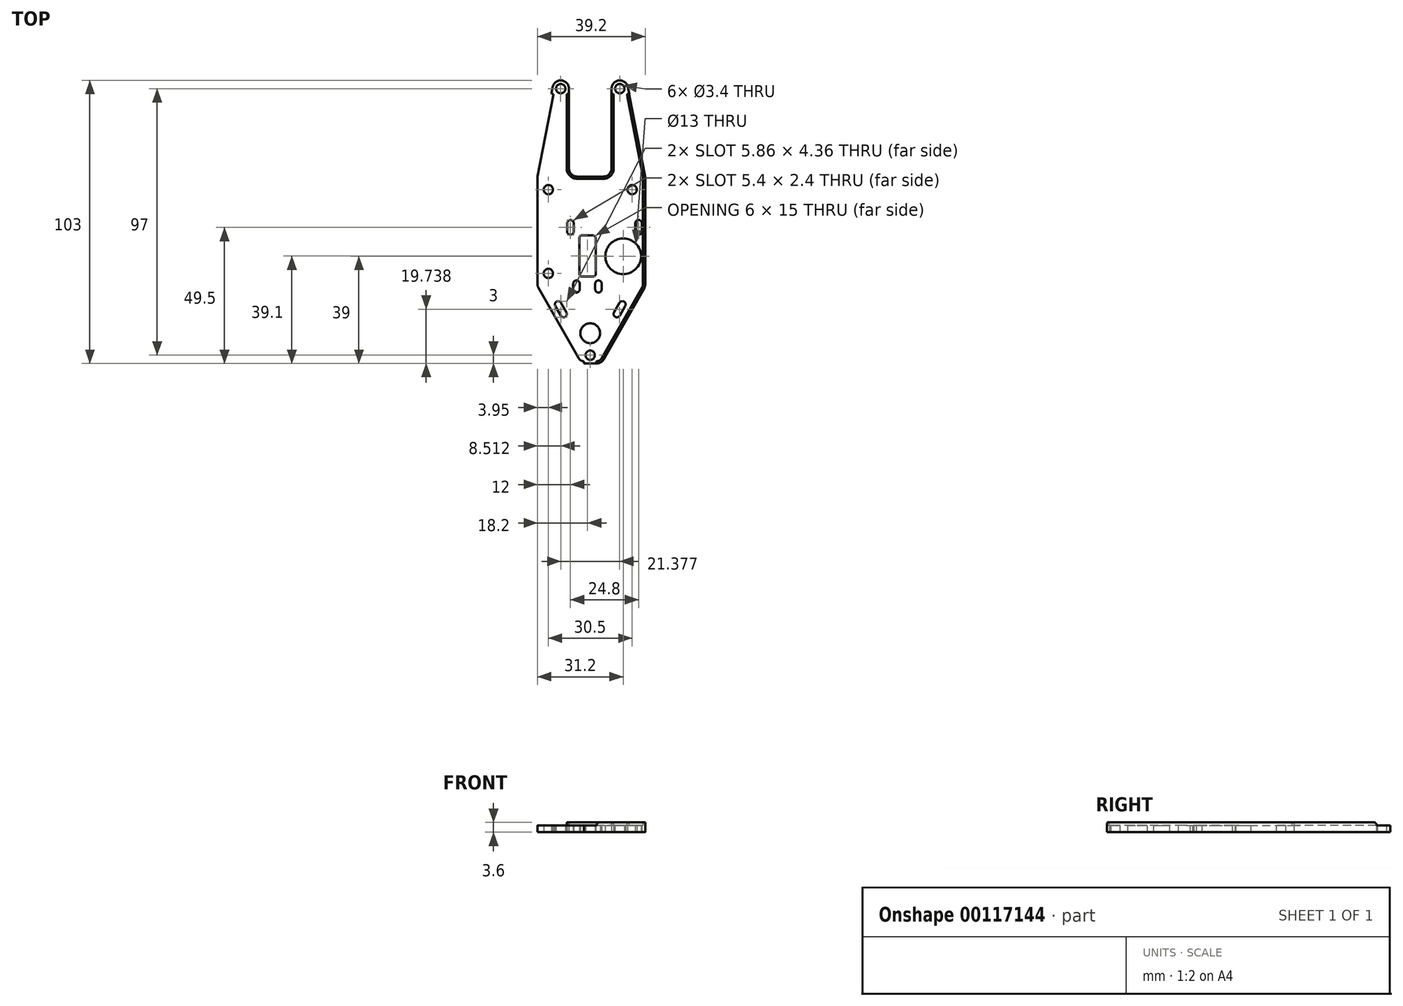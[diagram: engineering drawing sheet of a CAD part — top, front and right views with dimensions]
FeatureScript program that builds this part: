
annotation { "Feature Type Name" : "Feature", "Feature Type Description" : "" }
export const myFeature = defineFeature(function(context is Context, id is Id, definition is map)
    precondition{}
    {
        {
            var Q0;
            Q0=qCreatedBy(makeId("Top.planeOp"),FACE);
            var sketch = newSketch(context, id + "F0", { "sketchPlane" : qUnion([Q0])});
            skCircle(sketch, "E0", {"center": v(10.75, 52) * mm, "radius": 1.7 * mm});
            skCircle(sketch, "E1", {"center": v(15.25, 15.25) * mm, "radius": 1.7 * mm});
            skCircle(sketch, "E2", {"center": v(0, -45) * mm, "radius": 1.7 * mm});
            skCircle(sketch, "E3", {"center": v(0, -37) * mm, "radius": 3.6 * mm});
            skLineSegment(sketch, "E4", {"start": v(20, 0) * mm, "end": v(20, 19.71) * mm});
            skLineSegment(sketch, "E5", {"start": v(10.75, 55) * mm, "end": v(10.75, 55) * mm});
            skLineSegment(sketch, "E6", {"start": v(7.75, 52) * mm, "end": v(7.75, 23) * mm});
            skLineSegment(sketch, "E7", {"start": v(4.75, 20) * mm, "end": v(0, 20) * mm});
            skLineSegment(sketch, "E8", {"start": v(13.7, 52.57) * mm, "end": v(19.95, 20.28) * mm});
            skPoint(sketch, "E9.visualSharp", {"position": v(7.75, 55) * mm});
            skArc(sketch, "E9.filletArc", {"start": v(10.75, 55) * mm, "mid": v(8.63, 54.12) * mm, "end": v(7.75, 52) * mm});
            skPoint(sketch, "E10.visualSharp", {"position": v(13.22, 55) * mm});
            skArc(sketch, "E10.filletArc", {"start": v(13.7, 52.57) * mm, "mid": v(12.66, 54.31) * mm, "end": v(10.75, 55) * mm});
            skPoint(sketch, "E11.visualSharp", {"position": v(7.75, 20) * mm});
            skArc(sketch, "E11.filletArc", {"start": v(4.75, 20) * mm, "mid": v(6.87, 20.88) * mm, "end": v(7.75, 23) * mm});
            skCircle(sketch, "E12.MirrorC", {"center": v(15.25, -15.25) * mm, "radius": 1.7 * mm, "construction": true});
            skLineSegment(sketch, "E13.MirrorCS", {"start": v(20, 0) * mm, "end": v(20, -19.2) * mm});
            skLineSegment(sketch, "E14", {"start": v(0, -48) * mm, "end": v(2.3, -48) * mm});
            skLineSegment(sketch, "E15", {"start": v(19.6, -20.7) * mm, "end": v(4.9, -46.49) * mm});
            skPoint(sketch, "E16.visualSharp", {"position": v(4.05, -48) * mm});
            skArc(sketch, "E16.filletArc", {"start": v(2.3, -48) * mm, "mid": v(3.8, -47.6) * mm, "end": v(4.9, -46.49) * mm});
            skPoint(sketch, "E17.visualSharp", {"position": v(20, -20) * mm});
            skArc(sketch, "E17.filletArc", {"start": v(19.6, -20.7) * mm, "mid": v(19.9, -19.97) * mm, "end": v(20, -19.2) * mm});
            skLineSegment(sketch, "E18", {"start": v(9.7, -30) * mm, "end": v(11.68, -26.52) * mm, "construction": true});
            skArc(sketch, "E19.0.startCap", {"start": v(10.74, -30.6) * mm, "mid": v(9.1, -31.04) * mm, "end": v(8.66, -29.4) * mm});
            skArc(sketch, "E19.0.endCap", {"start": v(10.64, -25.93) * mm, "mid": v(12.27, -25.48) * mm, "end": v(12.72, -27.12) * mm});
            skLineSegment(sketch, "E19.0.left", {"start": v(8.66, -29.4) * mm, "end": v(10.64, -25.93) * mm});
            skLineSegment(sketch, "E19.0.right", {"start": v(10.74, -30.6) * mm, "end": v(12.72, -27.12) * mm});
            skPoint(sketch, "E20.visualSharp", {"position": v(20, 20) * mm});
            skArc(sketch, "E20.filletArc", {"start": v(20, 19.71) * mm, "mid": v(19.99, 20) * mm, "end": v(19.95, 20.28) * mm});
            skArc(sketch, "E21.MirrorCS", {"start": v(-19.6, -20.7) * mm, "mid": v(-19.9, -19.97) * mm, "end": v(-20, -19.2) * mm});
            skArc(sketch, "E22.MirrorCS", {"start": v(-20, 19.71) * mm, "mid": v(-19.99, 20) * mm, "end": v(-19.95, 20.28) * mm});
            skArc(sketch, "E23.MirrorCS", {"start": v(-10.74, -30.6) * mm, "mid": v(-9.1, -31.04) * mm, "end": v(-8.66, -29.4) * mm});
            skLineSegment(sketch, "E24.MirrorCS", {"start": v(-8.66, -29.4) * mm, "end": v(-10.64, -25.93) * mm});
            skArc(sketch, "E25.MirrorCS", {"start": v(-13.7, 52.57) * mm, "mid": v(-12.66, 54.31) * mm, "end": v(-10.75, 55) * mm});
            skCircle(sketch, "E26.MirrorC", {"center": v(-10.75, 52) * mm, "radius": 1.7 * mm});
            skArc(sketch, "E27.MirrorCS", {"start": v(-2.3, -48) * mm, "mid": v(-3.8, -47.6) * mm, "end": v(-4.9, -46.49) * mm});
            skLineSegment(sketch, "E28.MirrorCS", {"start": v(-9.7, -30) * mm, "end": v(-11.68, -26.52) * mm, "construction": true});
            skArc(sketch, "E29.MirrorCS", {"start": v(-10.64, -25.93) * mm, "mid": v(-12.27, -25.48) * mm, "end": v(-12.72, -27.12) * mm});
            skLineSegment(sketch, "E30.MirrorCS", {"start": v(-10.74, -30.6) * mm, "end": v(-12.72, -27.12) * mm});
            skArc(sketch, "E31.MirrorCS", {"start": v(-4.75, 20) * mm, "mid": v(-6.87, 20.88) * mm, "end": v(-7.75, 23) * mm});
            skArc(sketch, "E32.MirrorCS", {"start": v(-10.75, 55) * mm, "mid": v(-8.63, 54.12) * mm, "end": v(-7.75, 52) * mm});
            skLineSegment(sketch, "E33.MirrorCS", {"start": v(0, -48) * mm, "end": v(-2.3, -48) * mm});
            skPoint(sketch, "E34.MirrorP", {"position": v(-20, 20) * mm});
            skLineSegment(sketch, "E35.MirrorCS", {"start": v(-10.75, 55) * mm, "end": v(-10.75, 55) * mm});
            skLineSegment(sketch, "E36.MirrorCS", {"start": v(-20, 0) * mm, "end": v(-20, -19.2) * mm});
            skCircle(sketch, "E37.MirrorC", {"center": v(-15.25, -15.25) * mm, "radius": 1.7 * mm});
            skLineSegment(sketch, "E38.MirrorCS", {"start": v(-13.7, 52.57) * mm, "end": v(-19.95, 20.28) * mm});
            skLineSegment(sketch, "E39.MirrorCS", {"start": v(-4.75, 20) * mm, "end": v(0, 20) * mm});
            skLineSegment(sketch, "E40.MirrorCS", {"start": v(-20, 0) * mm, "end": v(-20, 19.71) * mm});
            skLineSegment(sketch, "E41.MirrorCS", {"start": v(-7.75, 52) * mm, "end": v(-7.75, 23) * mm});
            skCircle(sketch, "E42.MirrorC", {"center": v(-15.25, 15.25) * mm, "radius": 1.7 * mm});
            skPoint(sketch, "E43.MirrorP", {"position": v(-4.05, -48) * mm});
            skLineSegment(sketch, "E44.MirrorCS", {"start": v(-19.6, -20.7) * mm, "end": v(-4.9, -46.49) * mm});
            skPoint(sketch, "E45.MirrorP", {"position": v(-7.75, 55) * mm});
            skPoint(sketch, "E46.MirrorP", {"position": v(-13.22, 55) * mm});
            skPoint(sketch, "E47.MirrorP", {"position": v(-7.75, 20) * mm});
            skPoint(sketch, "E48.MirrorP", {"position": v(-20, -20) * mm});
            skLineSegment(sketch, "E49.bottom", {"start": v(-3, -1.4) * mm, "end": v(1, -1.4) * mm});
            skLineSegment(sketch, "E49.top", {"start": v(-3, -16.4) * mm, "end": v(1, -16.4) * mm});
            skLineSegment(sketch, "E49.left", {"start": v(-4, -2.4) * mm, "end": v(-4, -15.4) * mm});
            skLineSegment(sketch, "E49.right", {"start": v(2, -2.4) * mm, "end": v(2, -15.4) * mm});
            skPoint(sketch, "E50.visualSharp", {"position": v(-4, -1.4) * mm});
            skArc(sketch, "E50.filletArc", {"start": v(-3, -1.4) * mm, "mid": v(-3.7, -1.7) * mm, "end": v(-4, -2.4) * mm});
            skPoint(sketch, "E51.visualSharp", {"position": v(2, -16.4) * mm});
            skArc(sketch, "E51.filletArc", {"start": v(1, -16.4) * mm, "mid": v(1.7, -16.1) * mm, "end": v(2, -15.4) * mm});
            skPoint(sketch, "E52.visualSharp", {"position": v(-4, -16.4) * mm});
            skArc(sketch, "E52.filletArc", {"start": v(-4, -15.4) * mm, "mid": v(-3.7, -16.1) * mm, "end": v(-3, -16.4) * mm});
            skPoint(sketch, "E53.visualSharp", {"position": v(2, -1.4) * mm});
            skArc(sketch, "E53.filletArc", {"start": v(2, -2.4) * mm, "mid": v(1.7, -1.7) * mm, "end": v(1, -1.4) * mm});
            skCircle(sketch, "E54", {"center": v(12, -9) * mm, "radius": 6.5 * mm});
            skArc(sketch, "E55.0", {"start": v(18.91, -20.3) * mm, "mid": v(19.13, -19.77) * mm, "end": v(19.2, -19.2) * mm});
            skLineSegment(sketch, "E55.1", {"start": v(19.2, 0) * mm, "end": v(19.2, -19.2) * mm});
            skLineSegment(sketch, "E55.2", {"start": v(19.2, 0) * mm, "end": v(19.2, 19.71) * mm});
            skLineSegment(sketch, "E55.3", {"start": v(-13.38, 50) * mm, "end": v(-19.16, 20.13) * mm});
            skArc(sketch, "E55.4", {"start": v(-19.2, 19.71) * mm, "mid": v(-19.19, 19.92) * mm, "end": v(-19.16, 20.13) * mm});
            skLineSegment(sketch, "E55.5", {"start": v(-19.2, 0) * mm, "end": v(-19.2, 19.71) * mm});
            skLineSegment(sketch, "E55.6", {"start": v(-19.2, 0) * mm, "end": v(-19.2, -19.2) * mm});
            skArc(sketch, "E55.7", {"start": v(-18.91, -20.3) * mm, "mid": v(-19.13, -19.77) * mm, "end": v(-19.2, -19.2) * mm});
            skLineSegment(sketch, "E55.8", {"start": v(-18.91, -20.3) * mm, "end": v(-4.21, -46.09) * mm});
            skArc(sketch, "E55.9", {"start": v(2.3, -47.2) * mm, "mid": v(3.4, -46.9) * mm, "end": v(4.21, -46.09) * mm});
            skArc(sketch, "E55.12", {"start": v(-2.3, -47.2) * mm, "mid": v(-3.4, -46.9) * mm, "end": v(-4.21, -46.09) * mm});
            skLineSegment(sketch, "E55.15", {"start": v(-8.55, 50) * mm, "end": v(-8.55, 23) * mm});
            skLineSegment(sketch, "E55.16", {"start": v(18.91, -20.3) * mm, "end": v(4.21, -46.09) * mm});
            skArc(sketch, "E55.17", {"start": v(-4.75, 19.2) * mm, "mid": v(-7.44, 20.31) * mm, "end": v(-8.55, 23) * mm});
            skLineSegment(sketch, "E55.18", {"start": v(-4.75, 19.2) * mm, "end": v(0, 19.2) * mm});
            skLineSegment(sketch, "E55.19", {"start": v(4.75, 19.2) * mm, "end": v(0, 19.2) * mm});
            skArc(sketch, "E55.20", {"start": v(4.75, 19.2) * mm, "mid": v(7.44, 20.31) * mm, "end": v(8.55, 23) * mm});
            skLineSegment(sketch, "E55.21", {"start": v(8.55, 50) * mm, "end": v(8.55, 23) * mm});
            skLineSegment(sketch, "E55.24", {"start": v(13.38, 50) * mm, "end": v(19.16, 20.13) * mm});
            skArc(sketch, "E55.25", {"start": v(19.2, 19.71) * mm, "mid": v(19.19, 19.92) * mm, "end": v(19.16, 20.13) * mm});
            skLineSegment(sketch, "E56", {"start": v(-2.3, -47.2) * mm, "end": v(-2.3, -48) * mm});
            skLineSegment(sketch, "E57", {"start": v(2.3, -47.2) * mm, "end": v(2.3, -48) * mm});
            skLineSegment(sketch, "E58", {"start": v(-24.48, 50) * mm, "end": v(27.62, 50) * mm, "construction": true});
            skLineSegment(sketch, "E59", {"start": v(-8.55, 50) * mm, "end": v(-7.75, 50) * mm});
            skLineSegment(sketch, "E60", {"start": v(7.75, 50) * mm, "end": v(8.55, 50) * mm});
            skLineSegment(sketch, "E61", {"start": v(13.38, 50) * mm, "end": v(14.16, 50.15) * mm});
            skLineSegment(sketch, "E62", {"start": v(-13.38, 50) * mm, "end": v(-14.16, 50.15) * mm});
            skLineSegment(sketch, "E63", {"start": v(-7.2, 3) * mm, "end": v(-7.2, 0) * mm, "construction": true});
            skArc(sketch, "E64.0.startCap", {"start": v(-8.4, 3) * mm, "mid": v(-7.2, 4.2) * mm, "end": v(-6, 3) * mm});
            skArc(sketch, "E64.0.endCap", {"start": v(-6, 0) * mm, "mid": v(-7.2, -1.2) * mm, "end": v(-8.4, 0) * mm});
            skLineSegment(sketch, "E64.0.left", {"start": v(-6, 3) * mm, "end": v(-6, 0) * mm});
            skLineSegment(sketch, "E64.0.right", {"start": v(-8.4, 3) * mm, "end": v(-8.4, 0) * mm});
            skLineSegment(sketch, "E65", {"start": v(17.6, 0) * mm, "end": v(17.6, 3) * mm, "construction": true});
            skArc(sketch, "E66.0.startCap", {"start": v(18.8, 0) * mm, "mid": v(17.6, -1.2) * mm, "end": v(16.4, 0) * mm});
            skArc(sketch, "E66.0.endCap", {"start": v(16.4, 3) * mm, "mid": v(17.6, 4.2) * mm, "end": v(18.8, 3) * mm});
            skLineSegment(sketch, "E66.0.left", {"start": v(16.4, 0) * mm, "end": v(16.4, 3) * mm});
            skLineSegment(sketch, "E66.0.right", {"start": v(18.8, 0) * mm, "end": v(18.8, 3) * mm});
            skLineSegment(sketch, "E67", {"start": v(3, -19) * mm, "end": v(3, -21) * mm, "construction": true});
            skLineSegment(sketch, "E68", {"start": v(-5, -19) * mm, "end": v(-5, -21) * mm, "construction": true});
            skArc(sketch, "E69.0.startCap", {"start": v(1.8, -19) * mm, "mid": v(3, -17.8) * mm, "end": v(4.2, -19) * mm});
            skArc(sketch, "E69.0.endCap", {"start": v(4.2, -21) * mm, "mid": v(3, -22.2) * mm, "end": v(1.8, -21) * mm});
            skLineSegment(sketch, "E69.0.left", {"start": v(4.2, -19) * mm, "end": v(4.2, -21) * mm});
            skLineSegment(sketch, "E69.0.right", {"start": v(1.8, -19) * mm, "end": v(1.8, -21) * mm});
            skArc(sketch, "E69.1.startCap", {"start": v(-6.2, -19) * mm, "mid": v(-5, -17.8) * mm, "end": v(-3.8, -19) * mm});
            skArc(sketch, "E69.1.endCap", {"start": v(-3.8, -21) * mm, "mid": v(-5, -22.2) * mm, "end": v(-6.2, -21) * mm});
            skLineSegment(sketch, "E69.1.left", {"start": v(-3.8, -19) * mm, "end": v(-3.8, -21) * mm});
            skLineSegment(sketch, "E69.1.right", {"start": v(-6.2, -19) * mm, "end": v(-6.2, -21) * mm});
            skSolve(sketch);
        }
        {
            var Q0;
            Q0=makeQuery(id+"F0.imprint","IMPRINT",FACE,{"disambiguationData":[TD([[makeQuery(id+"F0.imprint","IMPRINT",EDGE,{"derivedFrom":sQuery(id+"F0.wireOp",EDGE,"E0")}),-1.0]])]});
            extrude(context, id + "F1", {"entities" : qUnion([Q0]), "depth" : 2.4 * mm});
        }
        {
            var Q0;
            Q0=makeQuery(id+"F0.imprint","IMPRINT",FACE,{"disambiguationData":[TD([[makeQuery(id+"F0.imprint","IMPRINT",EDGE,{"derivedFrom":sQuery(id+"F0.wireOp",EDGE,"E4")}),1.0]])]});
            var Q1;
            Q1=makeQuery(id+"F0.imprint","IMPRINT",FACE,{"disambiguationData":[TD([[makeQuery(id+"F0.imprint","IMPRINT",EDGE,{"derivedFrom":sQuery(id+"F0.wireOp",EDGE,"E7")}),1.0]])]});
            var Q2;
            Q2=makeQuery(id+"F0.imprint","IMPRINT",FACE,{"disambiguationData":[TD([[makeQuery(id+"F0.imprint","IMPRINT",EDGE,{"derivedFrom":sQuery(id+"F0.wireOp",EDGE,"E21.MirrorCS")}),-1.0]])]});
            extrude(context, id + "F2", {"entities" : qUnion([Q0, Q1, Q2]), "operationType" : NewBodyOperationType.ADD, "depth" : 3.6 * mm});
        }
        {
            var Q0;
            Q0=makeQuery(id+"F2.opExtrude","CAP_EDGE",EDGE,{"disambiguationData":[OSD([sQuery(id+"F0.wireOp",EDGE,"E62")])],"isStart":false});
            var Q1;
            Q1=makeQuery(id+"F2.opExtrude","CAP_EDGE",EDGE,{"disambiguationData":[OSD([sQuery(id+"F0.wireOp",EDGE,"E59")])],"isStart":false});
            var Q2;
            Q2=makeQuery(id+"F2.opExtrude","CAP_EDGE",EDGE,{"disambiguationData":[OSD([sQuery(id+"F0.wireOp",EDGE,"E60")])],"isStart":false});
            var Q3;
            Q3=makeQuery(id+"F2.opExtrude","CAP_EDGE",EDGE,{"disambiguationData":[OSD([sQuery(id+"F0.wireOp",EDGE,"E61")])],"isStart":false});
            var Q4;
            Q4=makeQuery(id+"F2.opExtrude","CAP_EDGE",EDGE,{"disambiguationData":[OSD([sQuery(id+"F0.wireOp",EDGE,"E56")])],"isStart":false});
            var Q5;
            Q5=makeQuery(id+"F2.opExtrude","CAP_EDGE",EDGE,{"disambiguationData":[OSD([sQuery(id+"F0.wireOp",EDGE,"E57")])],"isStart":false});
            fillet(context, id + "F3", {"entities" : qUnion([Q0, Q1, Q2, Q3, Q4, Q5]), "radius" : 1.2 * mm, "tangentPropagation" : true, "allowEdgeOverflow" : false});
        }
    });
